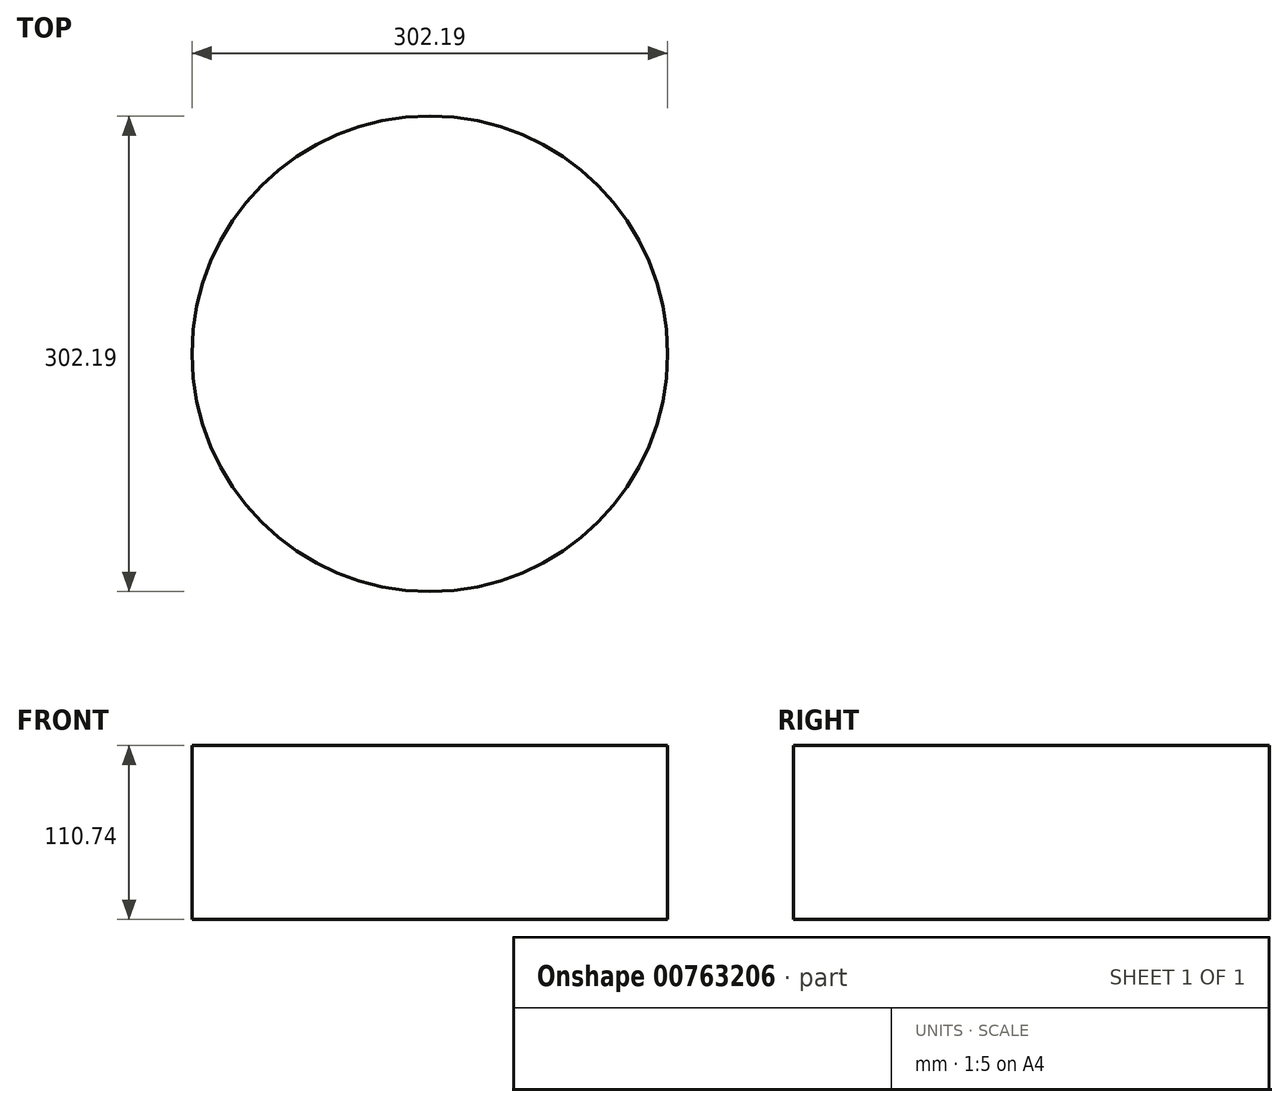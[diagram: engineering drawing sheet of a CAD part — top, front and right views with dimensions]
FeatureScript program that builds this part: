
annotation { "Feature Type Name" : "Feature", "Feature Type Description" : "" }
export const myFeature = defineFeature(function(context is Context, id is Id, definition is map)
    precondition{}
    {
        {
            var Q0;
            Q0=qCreatedBy(makeId("Top.planeOp"),FACE);
            var sketch = newSketch(context, id + "F0", { "sketchPlane" : qUnion([Q0])});
            skCircle(sketch, "E0", {"center": v(-79.59, 31.67) * mm, "radius": 151.1 * mm});
            skSolve(sketch);
        }
        {
            var Q0;
            Q0=makeQuery(id+"F0.imprint","IMPRINT",FACE,{"disambiguationData":[TD([[makeQuery(id+"F0.imprint","IMPRINT",EDGE,{"derivedFrom":sQuery(id+"F0.wireOp",EDGE,"E0")}),1.0]])]});
            extrude(context, id + "F1", {"entities" : qUnion([Q0]), "depth" : 110.74 * mm, "offsetDistance" : 25.4 * mm});
        }
    });
